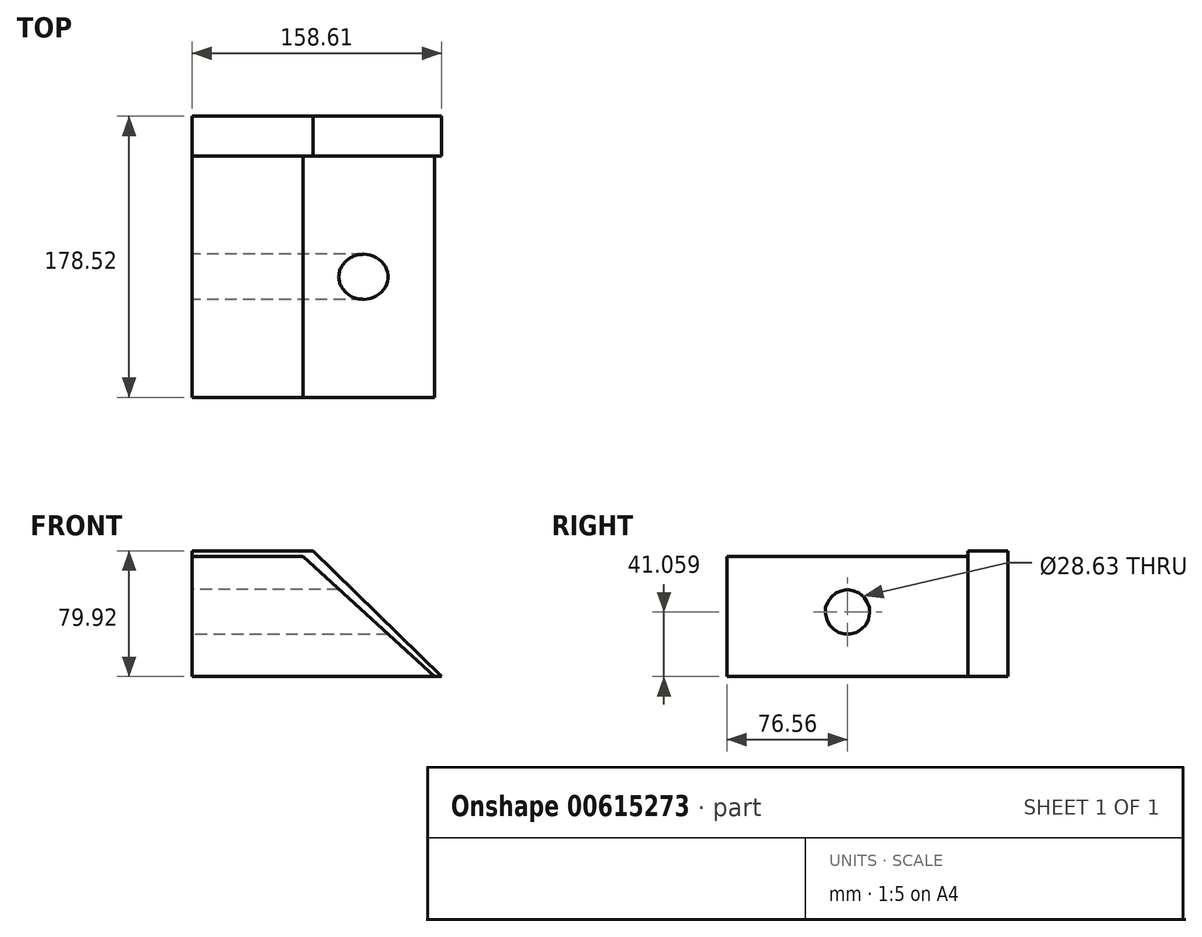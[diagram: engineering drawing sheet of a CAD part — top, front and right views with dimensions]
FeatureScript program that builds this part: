
annotation { "Feature Type Name" : "Feature", "Feature Type Description" : "" }
export const myFeature = defineFeature(function(context is Context, id is Id, definition is map)
    precondition{}
    {
        {
            var Q0;
            Q0=qCreatedBy(makeId("Top.planeOp"),FACE);
            var sketch = newSketch(context, id + "F0", { "sketchPlane" : qUnion([Q0])});
            skLineSegment(sketch, "E0.bottom", {"start": v(-76.95, -76.56) * mm, "end": v(76.95, -76.56) * mm});
            skLineSegment(sketch, "E0.top", {"start": v(-76.95, 76.56) * mm, "end": v(76.95, 76.56) * mm});
            skLineSegment(sketch, "E0.left", {"start": v(-76.95, -76.56) * mm, "end": v(-76.95, 76.56) * mm});
            skLineSegment(sketch, "E0.right", {"start": v(76.95, -76.56) * mm, "end": v(76.95, 76.56) * mm});
            skPoint(sketch, "E0.middle", {"position": v(0, 0) * mm});
            skSolve(sketch);
        }
        {
            var Q0;
            Q0=makeQuery(id+"F0.imprint","IMPRINT",FACE,{"disambiguationData":[TD([[makeQuery(id+"F0.imprint","IMPRINT",EDGE,{"derivedFrom":sQuery(id+"F0.wireOp",EDGE,"E0.bottom")}),1.0]])]});
            extrude(context, id + "F1", {"entities" : qUnion([Q0]), "depth" : 76.2 * mm, "offsetDistance" : 25.4 * mm});
        }
        {
            var Q0;
            Q0=makeQuery(id+"F1.opExtrude","SWEPT_FACE",FACE,{"disambiguationData":[OSD([sQuery(id+"F0.wireOp",EDGE,"E0.bottom")])]});
            var sketch = newSketch(context, id + "F2", { "sketchPlane" : qUnion([Q0])});
            skLineSegment(sketch, "E1", {"start": v(-6.5, 76.2) * mm, "end": v(76.95, 76.2) * mm});
            skLineSegment(sketch, "E2", {"start": v(76.95, 76.2) * mm, "end": v(76.95, 0) * mm});
            skLineSegment(sketch, "E3", {"start": v(76.95, 0) * mm, "end": v(-6.5, 76.2) * mm});
            skSolve(sketch);
        }
        {
            var Q0;
            Q0=makeQuery(id+"F2.imprint","IMPRINT",FACE,{"disambiguationData":[TD([[makeQuery(id+"F2.imprint","IMPRINT",EDGE,{"derivedFrom":sQuery(id+"F2.wireOp",EDGE,"E1")}),-1.0]])]});
            extrude(context, id + "F3", {"entities" : qUnion([Q0]), "operationType" : NewBodyOperationType.REMOVE, "endBound" : BoundingType.SYMMETRIC, "oppositeDirection" : true, "depth" : 508 * mm, "offsetDistance" : 25.4 * mm});
        }
        {
            var Q0;
            Q0=makeQuery(id+"F1.opExtrude","SWEPT_FACE",FACE,{"disambiguationData":[OSD([sQuery(id+"F0.wireOp",EDGE,"E0.left")])]});
            var sketch = newSketch(context, id + "F4", { "sketchPlane" : qUnion([Q0])});
            skCircle(sketch, "E4", {"center": v(0, 41.06) * mm, "radius": 14.32 * mm});
            skSolve(sketch);
        }
        {
            var Q0;
            Q0=makeQuery(id+"F4.imprint","IMPRINT",FACE,{"disambiguationData":[TD([[makeQuery(id+"F4.imprint","IMPRINT",EDGE,{"derivedFrom":sQuery(id+"F4.wireOp",EDGE,"E4")}),1.0]])]});
            extrude(context, id + "F5", {"entities" : qUnion([Q0]), "operationType" : NewBodyOperationType.REMOVE, "oppositeDirection" : true, "depth" : 508 * mm, "offsetDistance" : 25.4 * mm});
        }
        {
            var Q0;
            Q0=makeQuery(id+"F1.opExtrude","SWEPT_FACE",FACE,{"disambiguationData":[OSD([sQuery(id+"F0.wireOp",EDGE,"E0.top")])]});
            var sketch = newSketch(context, id + "F6", { "sketchPlane" : qUnion([Q0])});
            skLineSegment(sketch, "E5.bottom", {"start": v(76.95, 0) * mm, "end": v(-81.66, 0) * mm});
            skLineSegment(sketch, "E5.top", {"start": v(76.95, 79.92) * mm, "end": v(-81.66, 79.92) * mm});
            skLineSegment(sketch, "E5.left", {"start": v(76.95, 0) * mm, "end": v(76.95, 79.92) * mm});
            skLineSegment(sketch, "E5.right", {"start": v(-81.66, 0) * mm, "end": v(-81.66, 79.92) * mm});
            skSolve(sketch);
        }
        {
            var Q0;
            {var subQ4=sQuery(id+"F6.wireOp",EDGE,"E5.top");Q0=makeQuery(id+"F6.imprint","IMPRINT",FACE,{"disambiguationData":[TD([[makeQuery(id+"F6.imprint","IMPRINT",EDGE,{"derivedFrom":subQ4}),1.0]])]});}
            var Q1;
            {var subQ3=sQuery(id+"F0.wireOp",EDGE,"E0.top");var subQ5=makeQuery(id+"F1.opExtrude","CAP_EDGE",EDGE,{"disambiguationData":[OSD([subQ3])],"isStart":false});Q1=makeQuery(id+"F6.imprint","IMPRINT",FACE,{"disambiguationData":[TD([[makeQuery(id+"F6.imprint","IMPRINT",EDGE,{"derivedFrom":subQ5}),1.0]])]});}
            extrude(context, id + "F7", {"entities" : qUnion([Q0, Q1]), "operationType" : NewBodyOperationType.ADD, "depth" : 25.4 * mm, "offsetDistance" : 25.4 * mm});
        }
        {
            var Q0;
            Q0=makeQuery(id+"F7.opExtrude","CAP_FACE",FACE,{"disambiguationData":[OSD([sQuery(id+"F6.wireOp",EDGE,"E5.bottom"),sQuery(id+"F6.wireOp",EDGE,"E5.top"),sQuery(id+"F6.wireOp",EDGE,"E5.left"),sQuery(id+"F6.wireOp",EDGE,"E5.right")])],"isStart":true});
            var sketch = newSketch(context, id + "F8", { "sketchPlane" : qUnion([Q0])});
            skLineSegment(sketch, "E6", {"start": v(81.66, 0) * mm, "end": v(0, 79.92) * mm});
            skLineSegment(sketch, "E7", {"start": v(0, 79.92) * mm, "end": v(81.66, 79.92) * mm});
            skLineSegment(sketch, "E8", {"start": v(81.66, 79.92) * mm, "end": v(81.66, 0) * mm});
            skSolve(sketch);
        }
        {
            var Q0;
            Q0=makeQuery(id+"F8.imprint","IMPRINT",FACE,{"disambiguationData":[TD([[makeQuery(id+"F8.imprint","IMPRINT",EDGE,{"derivedFrom":sQuery(id+"F8.wireOp",EDGE,"E6")}),-1.0]])]});
            extrude(context, id + "F9", {"entities" : qUnion([Q0]), "operationType" : NewBodyOperationType.REMOVE, "endBound" : BoundingType.SYMMETRIC, "oppositeDirection" : true, "depth" : 127 * mm, "offsetDistance" : 25.4 * mm});
        }
    });
